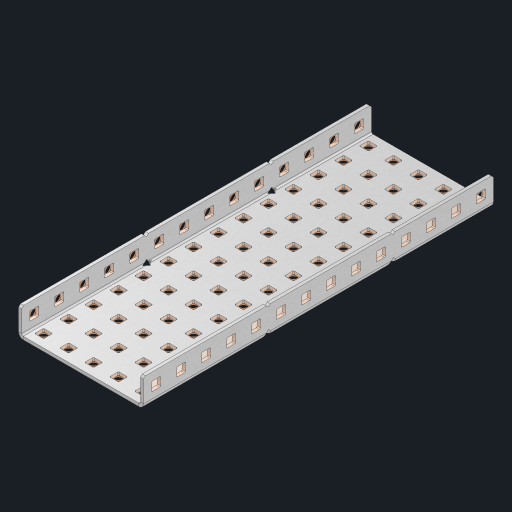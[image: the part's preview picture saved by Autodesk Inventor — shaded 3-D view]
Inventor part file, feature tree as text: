
AUTODESK INVENTOR PART (.ipt)
format: ipt  version: 2023 (Build 270158000, 158)  size: 1,269,248 bytes
history: native  units: in
note: dims shown in document units (in); Inventor stores cm internally (conversion verified against a paired STEP export)
features: other x103, extrude x97, sheet_metal_op x10, sketch x8, mirror x1, pattern_linear x1, chamfer x1
ambient origin geometry x8: Origin, YZ Plane, XZ Plane, XY Plane, X Axis, Y Axis, Z Axis, Center Point
bodies: Solid1 (feature_tree), Body (feature_tree)
feature tree (221):
  other  "Flange Pattern Plane"
  sheet_metal_op  "Flange Pattern"
  sheet_metal_op  "Body Pattern"
  other  "Arc Length"
  mirror  "Notch Mirror"
  pattern_linear  "Notch Pattern"  Spacing1=0.25in  [1 undecoded]
  chamfer  "End Chamfer"
  extrude  "Half Cut"  Depth=0.0625in
  sketch  "Sketch1"  dims[d0=2.5in]
  other  "Plate1"
  sketch  "Sketch2"  dims[d1=7.0in]
  other  "Plate2"
  sheet_metal_op  "Bend1"
  sheet_metal_op  "Corner1"
  sketch  "Sketch3"  dims[d2=0.0625in]
  other  "Flange Pattern Sketch"
  sketch  "Sketch7"  dims[d3=0.0625in]
  other  "Srf1"
  other  "Srf2"
  sketch  "Sketch8"  dims[d4=0.0312in]
  sketch  "Sketch9"  dims[d5=0.125in]
  other  "Srf91"
  sheet_metal_op  "Body Pattern Sketch"
  other  "Srf92"
  sketch  "Sketch13"  dims[d6=0.0625in]
  sketch  "Sketch14"  dims[d7=0.5in d8=90.0deg d9=0.0312in d10=0.25in d11=0.0625in d12=0.0625in d16=0.182in d17=0.02in d18=0.0625in d19=0.0in d20=0.25in d21=0.25in d46=0.172in d47=1.0in d48=0.0in d49=0.182in d50=0.02in d51=0.25in d52=0.25in d53=0.0625in d54=0.0in d55=0.172in d56=1.0in d57=0.0in d60=5.5118in d62=0.5in d63=1.9685in d65=0.5in d85=0.1473in d86=0.1782in d88=0.04in d89=0.0625in d90=0.0in d91=0.04in d92=0.0491in d95=2.5in d96=0.04in d97=0.25in d98=45.0deg d101=0.0in d102=2.497in d131=2.5in d132=5.5118in d134=0.5in d139=0.5in]
  other  "Srf856"
  other  "Srf1310"
  other  "Srf1311"
  other  "Srf1312"
  other  "Srf1376"
  other  "Srf1377"
  other  "Srf1728"
  other  "Srf1755"
  other  "Srf1878"
  other  "Srf1879"
  other  "Srf1880"
  other  "Srf1881"
  other  "Srf1882"
  other  "Srf1883"
  other  "Srf1884"
  other  "Srf1885"
  other  "Srf1886"
  other  "Srf1887"
  other  "Srf1888"
  other  "Srf1889"
  other  "Srf1890"
  other  "Srf1891"
  other  "Srf1892"
  other  "Srf1893"
  other  "Srf1894"
  other  "Srf1895"
  other  "Srf1896"
  other  "Srf1897"
  other  "Srf1898"
  other  "Srf1899"
  other  "Srf1942"
  other  "Srf1943"
  other  "Srf1944"
  other  "Srf1945"
  other  "Srf1946"
  other  "Srf1947"
  other  "Srf1948"
  other  "Srf1949"
  other  "Srf1950"
  other  "Srf1951"
  other  "Srf1952"
  other  "Srf1953"
  other  "Srf1954"
  other  "Srf1955"
  other  "Srf1956"
  other  "Srf1957"
  other  "Srf1958"
  other  "Srf1959"
  other  "Srf1960"
  other  "Srf1961"
  other  "Srf1962"
  other  "Srf1963"
  other  "Srf1964"
  other  "Srf1965"
  other  "Srf1966"
  other  "Srf1967"
  other  "Srf1968"
  other  "Srf1969"
  other  "Srf1970"
  other  "Srf2146"
  other  "Srf2147"
  other  "Srf2148"
  other  "Srf2149"
  other  "Srf2150"
  other  "Srf2151"
  other  "Srf2152"
  other  "Srf2153"
  other  "Srf2154"
  other  "Srf2155"
  other  "Srf2156"
  other  "Srf2157"
  other  "Srf2158"
  other  "Srf2159"
  other  "Srf2160"
  other  "Srf2161"
  other  "Srf2162"
  other  "Srf2163"
  other  "Srf2164"
  other  "Srf2165"
  other  "Srf2166"
  other  "Srf2167"
  other  "Srf2168"
  other  "Srf2169"
  other  "Srf2170"
  other  "Srf2171"
  other  "Srf2172"
  other  "Srf2173"
  other  "Srf2174"
  other  "Srf2175"
  other  "Srf2176"
  other  "Srf2177"
  other  "Srf2178"
  other  "Srf2179"
  other  "Srf2180"
  sheet_metal_op  "Flange Stamp"
  sheet_metal_op  "Flange Circle"
  sheet_metal_op  "Body Stamp"
  sheet_metal_op  "Body Circle"
  sheet_metal_op  "Notch"
  extrude  "ExtrusionSrf2"  Depth=0.0625in
  extrude  "ExtrusionSrf92"  Depth=2.5in
  extrude  "ExtrusionSrf856"  Depth=0.02in
  extrude  "ExtrusionSrf1310"  Depth=0.0625in
  extrude  "ExtrusionSrf1311"  TaperAngle=0.0deg  [1 undecoded]
  extrude  "ExtrusionSrf1312"  Depth=0.25in
  extrude  "ExtrusionSrf1376"  Depth=0.25in
  extrude  "ExtrusionSrf1377"  Depth=2.5in
  extrude  "ExtrusionSrf1728"  Depth=2.5in TaperAngle=0.0deg
  extrude  "ExtrusionSrf1755"  Depth=2.5in
  extrude  "ExtrusionSrf1878"  Depth=0.02in
  extrude  "ExtrusionSrf1879"  Depth=0.25in
  extrude  "ExtrusionSrf1880"  Depth=0.25in
  extrude  "ExtrusionSrf1881"  Depth=0.0625in
  extrude  "ExtrusionSrf1882"  TaperAngle=0.0deg  [1 undecoded]
  extrude  "ExtrusionSrf1883"  Depth=2.5in
  extrude  "ExtrusionSrf1884"  Depth=2.5in TaperAngle=0.0deg
  extrude  "ExtrusionSrf1885"  Depth=2.5in
  extrude  "ExtrusionSrf1886"  Depth=2.5in
  extrude  "ExtrusionSrf1887"  Depth=2.5in
  extrude  "ExtrusionSrf1888"  Depth=2.5in
  extrude  "ExtrusionSrf1889"  Depth=2.5in
  extrude  "ExtrusionSrf1890"  Depth=0.0625in
  extrude  "ExtrusionSrf1891"  TaperAngle=0.0deg  [1 undecoded]
  extrude  "ExtrusionSrf1892"  Depth=2.5in
  extrude  "ExtrusionSrf1893"  Depth=2.5in
  extrude  "ExtrusionSrf1894"  Depth=2.5in
  extrude  "ExtrusionSrf1895"  Depth=0.25in TaperAngle=45.0deg
  extrude  "ExtrusionSrf1896"  TaperAngle=0.0deg  [1 undecoded]
  extrude  "ExtrusionSrf1897"  Depth=2.5in
  extrude  "ExtrusionSrf1898"  Depth=2.5in
  extrude  "ExtrusionSrf1899"  Depth=2.5in
  extrude  "ExtrusionSrf1942"  Depth=2.5in
  extrude  "ExtrusionSrf1943"  Depth=2.5in
  extrude  "ExtrusionSrf1944"  [1 undecoded]
  extrude  "ExtrusionSrf1945"  [1 undecoded]
  extrude  "ExtrusionSrf1946"  [1 undecoded]
  extrude  "ExtrusionSrf1947"  [1 undecoded]
  extrude  "ExtrusionSrf1948"  [1 undecoded]
  extrude  "ExtrusionSrf1949"  [1 undecoded]
  extrude  "ExtrusionSrf1950"  [1 undecoded]
  extrude  "ExtrusionSrf1951"  [1 undecoded]
  extrude  "ExtrusionSrf1952"  [1 undecoded]
  extrude  "ExtrusionSrf1953"  [1 undecoded]
  extrude  "ExtrusionSrf1954"  [1 undecoded]
  extrude  "ExtrusionSrf1955"  [1 undecoded]
  extrude  "ExtrusionSrf1956"  [1 undecoded]
  extrude  "ExtrusionSrf1957"  [1 undecoded]
  extrude  "ExtrusionSrf1958"  [1 undecoded]
  extrude  "ExtrusionSrf1959"  [1 undecoded]
  extrude  "ExtrusionSrf1960"  [1 undecoded]
  extrude  "ExtrusionSrf1961"  [1 undecoded]
  extrude  "ExtrusionSrf1962"  [1 undecoded]
  extrude  "ExtrusionSrf1963"  [1 undecoded]
  extrude  "ExtrusionSrf1964"  [1 undecoded]
  extrude  "ExtrusionSrf1965"  [1 undecoded]
  extrude  "ExtrusionSrf1966"  [1 undecoded]
  extrude  "ExtrusionSrf1967"  [1 undecoded]
  extrude  "ExtrusionSrf1968"  [1 undecoded]
  extrude  "ExtrusionSrf1969"  [1 undecoded]
  extrude  "ExtrusionSrf1970"  [1 undecoded]
  extrude  "ExtrusionSrf2146"  [1 undecoded]
  extrude  "ExtrusionSrf2147"  [1 undecoded]
  extrude  "ExtrusionSrf2148"  [1 undecoded]
  extrude  "ExtrusionSrf2149"  [1 undecoded]
  extrude  "ExtrusionSrf2150"  [1 undecoded]
  extrude  "ExtrusionSrf2151"  [1 undecoded]
  extrude  "ExtrusionSrf2152"  [1 undecoded]
  extrude  "ExtrusionSrf2153"  [1 undecoded]
  extrude  "ExtrusionSrf2154"  [1 undecoded]
  extrude  "ExtrusionSrf2155"  [1 undecoded]
  extrude  "ExtrusionSrf2156"  [1 undecoded]
  extrude  "ExtrusionSrf2157"  [1 undecoded]
  extrude  "ExtrusionSrf2158"  [1 undecoded]
  extrude  "ExtrusionSrf2159"  [1 undecoded]
  extrude  "ExtrusionSrf2160"  [1 undecoded]
  extrude  "ExtrusionSrf2161"  [1 undecoded]
  extrude  "ExtrusionSrf2162"  [1 undecoded]
  extrude  "ExtrusionSrf2163"  [1 undecoded]
  extrude  "ExtrusionSrf2164"  [1 undecoded]
  extrude  "ExtrusionSrf2165"  [1 undecoded]
  extrude  "ExtrusionSrf2166"  [1 undecoded]
  extrude  "ExtrusionSrf2167"  [1 undecoded]
  extrude  "ExtrusionSrf2168"  [1 undecoded]
  extrude  "ExtrusionSrf2169"  [1 undecoded]
  extrude  "ExtrusionSrf2170"  [1 undecoded]
  extrude  "ExtrusionSrf2171"  [1 undecoded]
  extrude  "ExtrusionSrf2172"  [1 undecoded]
  extrude  "ExtrusionSrf2173"  [1 undecoded]
  extrude  "ExtrusionSrf2174"  [1 undecoded]
  extrude  "ExtrusionSrf2175"  [1 undecoded]
  extrude  "ExtrusionSrf2176"  [1 undecoded]
  extrude  "ExtrusionSrf2177"  [1 undecoded]
  extrude  "ExtrusionSrf2178"  [1 undecoded]
  extrude  "ExtrusionSrf2179"  [1 undecoded]
  extrude  "ExtrusionSrf2180"  [1 undecoded]
note: 67 required parameter values undecoded (feature->parameter linkage not recoverable at this tier; creation-order binding heuristic only, values carry confidence <= 0.55)
